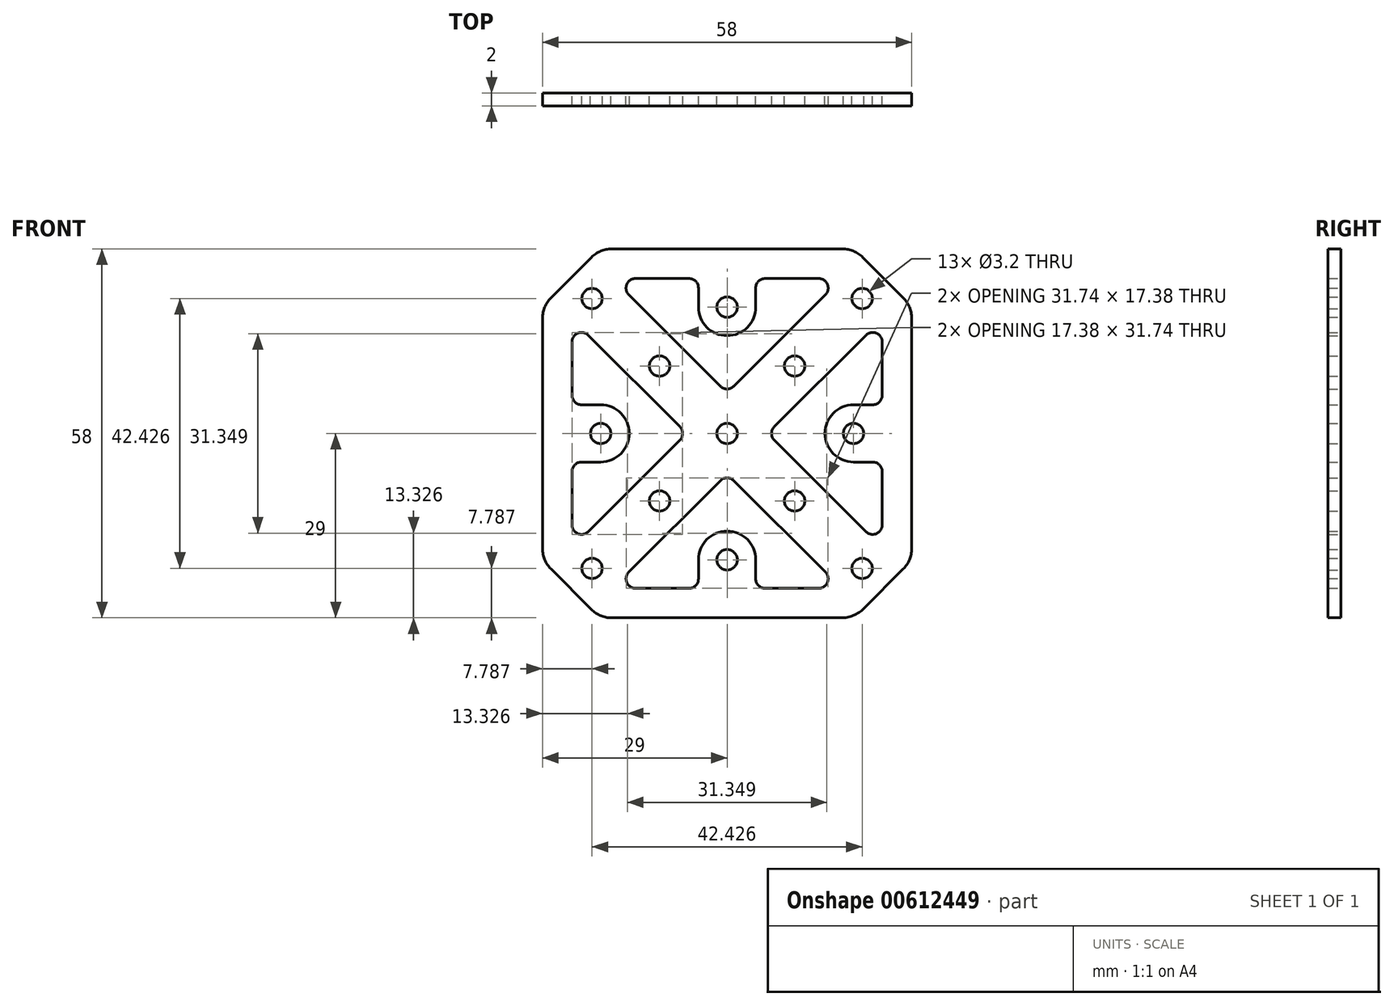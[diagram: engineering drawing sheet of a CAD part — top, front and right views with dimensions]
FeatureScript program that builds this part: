
annotation { "Feature Type Name" : "Feature", "Feature Type Description" : "" }
export const myFeature = defineFeature(function(context is Context, id is Id, definition is map)
    precondition{}
    {
        {
            var Q0;
            Q0=qCreatedBy(makeId("Front.planeOp"),FACE);
            var sketch = newSketch(context, id + "F0", { "sketchPlane" : qUnion([Q0])});
            skLineSegment(sketch, "E0.bottom", {"start": v(0, 0) * mm, "end": v(58, 0) * mm, "construction": true});
            skLineSegment(sketch, "E0.top", {"start": v(0, 58) * mm, "end": v(58, 58) * mm, "construction": true});
            skLineSegment(sketch, "E0.left", {"start": v(0, 0) * mm, "end": v(0, 58) * mm, "construction": true});
            skLineSegment(sketch, "E0.right", {"start": v(58, 0) * mm, "end": v(58, 58) * mm, "construction": true});
            skLineSegment(sketch, "E1", {"start": v(0, 58) * mm, "end": v(58, 0) * mm, "construction": true});
            skCircle(sketch, "E2", {"center": v(29, 29) * mm, "radius": 1.6 * mm});
            skCircle(sketch, "E3", {"center": v(39.6, 18.4) * mm, "radius": 1.6 * mm});
            skCircle(sketch, "E4", {"center": v(50.21, 7.79) * mm, "radius": 1.6 * mm});
            skLineSegment(sketch, "E5", {"start": v(29, 29) * mm, "end": v(29, 0) * mm, "construction": true});
            skLineSegment(sketch, "E6", {"start": v(58, 9) * mm, "end": v(49, 0) * mm, "construction": true});
            skLineSegment(sketch, "E7.MirrorCS", {"start": v(0, 9) * mm, "end": v(9, 0) * mm, "construction": true});
            skLineSegment(sketch, "E8", {"start": v(29, 22.64) * mm, "end": v(47, 4.64) * mm, "construction": true});
            skLineSegment(sketch, "E9", {"start": v(47, 4.64) * mm, "end": v(29, 4.64) * mm, "construction": true});
            skLineSegment(sketch, "E10", {"start": v(29, 4.64) * mm, "end": v(29, 22.64) * mm});
            skLineSegment(sketch, "E11.MirrorCS", {"start": v(11, 4.64) * mm, "end": v(29, 4.64) * mm, "construction": true});
            skLineSegment(sketch, "E12.MirrorCS", {"start": v(29, 22.64) * mm, "end": v(11, 4.64) * mm, "construction": true});
            skLineSegment(sketch, "E13", {"start": v(29, 29) * mm, "end": v(0, 29) * mm, "construction": true});
            skLineSegment(sketch, "E14.MirrorCS", {"start": v(0, 49) * mm, "end": v(9, 58) * mm, "construction": true});
            skLineSegment(sketch, "E15.MirrorCS", {"start": v(58, 49) * mm, "end": v(49, 58) * mm, "construction": true});
            skLineSegment(sketch, "E16", {"start": v(24.5, 9.14) * mm, "end": v(24.5, 4.64) * mm, "construction": true});
            skLineSegment(sketch, "E17", {"start": v(33.5, 9.14) * mm, "end": v(33.5, 4.64) * mm, "construction": true});
            skArc(sketch, "E18", {"start": v(24.5, 9.14) * mm, "mid": v(29, 4.64) * mm, "end": v(33.5, 9.14) * mm, "construction": true});
            skArc(sketch, "E19", {"start": v(33.5, 9.14) * mm, "mid": v(29, 13.64) * mm, "end": v(24.5, 9.14) * mm, "construction": true});
            skCircle(sketch, "E20", {"center": v(29, 9.14) * mm, "radius": 1.6 * mm});
            skSolve(sketch);
        }
        {
            var Q0;
            Q0=qCreatedBy(makeId("Front.planeOp"),FACE);
            var sketch = newSketch(context, id + "F1", { "sketchPlane" : qUnion([Q0])});
            skLineSegment(sketch, "E21.0", {"start": v(10.86, 58) * mm, "end": v(47.14, 58) * mm});
            skLineSegment(sketch, "E21.1", {"start": v(1.32, 50.32) * mm, "end": v(7.68, 56.68) * mm});
            skLineSegment(sketch, "E21.2", {"start": v(0, 10.86) * mm, "end": v(0, 47.14) * mm});
            skLineSegment(sketch, "E21.3", {"start": v(1.32, 7.68) * mm, "end": v(7.68, 1.32) * mm});
            skLineSegment(sketch, "E21.4", {"start": v(10.86, 0) * mm, "end": v(46.93, 0) * mm});
            skLineSegment(sketch, "E21.5", {"start": v(56.68, 7.68) * mm, "end": v(50.46, 1.46) * mm});
            skLineSegment(sketch, "E21.6", {"start": v(58, 10.86) * mm, "end": v(58, 47.14) * mm});
            skCircle(sketch, "E21.7", {"center": v(50.21, 7.79) * mm, "radius": 1.6 * mm});
            skCircle(sketch, "E21.8", {"center": v(39.6, 18.4) * mm, "radius": 1.6 * mm});
            skCircle(sketch, "E21.9", {"center": v(29, 29) * mm, "radius": 1.6 * mm});
            skArc(sketch, "E21.10", {"start": v(33.5, 9.14) * mm, "mid": v(29, 13.64) * mm, "end": v(24.5, 9.14) * mm});
            skLineSegment(sketch, "E21.11", {"start": v(24.5, 9.14) * mm, "end": v(24.5, 6.14) * mm});
            skLineSegment(sketch, "E21.12", {"start": v(33.5, 9.14) * mm, "end": v(33.5, 6.14) * mm});
            skLineSegment(sketch, "E21.13", {"start": v(43.38, 4.64) * mm, "end": v(35, 4.64) * mm});
            skLineSegment(sketch, "E21.14", {"start": v(30.06, 21.58) * mm, "end": v(44.44, 7.2) * mm});
            skLineSegment(sketch, "E21.15", {"start": v(27.94, 21.58) * mm, "end": v(13.56, 7.2) * mm});
            skLineSegment(sketch, "E21.16", {"start": v(14.62, 4.64) * mm, "end": v(23, 4.64) * mm});
            skPoint(sketch, "E22.orphan", {"position": v(0, 58) * mm});
            skLineSegment(sketch, "E23.0", {"start": v(56.68, 50.32) * mm, "end": v(50.32, 56.68) * mm});
            skPoint(sketch, "E24.orphan", {"position": v(58, 58) * mm});
            skPoint(sketch, "E25.orphan", {"position": v(58, 0) * mm});
            skPoint(sketch, "E26.orphan", {"position": v(0, 0) * mm});
            skPoint(sketch, "E27.visualSharp", {"position": v(47, 4.64) * mm});
            skArc(sketch, "E27.filletArc", {"start": v(43.38, 4.64) * mm, "mid": v(44.76, 5.56) * mm, "end": v(44.44, 7.2) * mm});
            skPoint(sketch, "E28.visualSharp", {"position": v(29, 22.64) * mm});
            skArc(sketch, "E28.filletArc", {"start": v(30.06, 21.58) * mm, "mid": v(29, 22.02) * mm, "end": v(27.94, 21.58) * mm});
            skPoint(sketch, "E29.visualSharp", {"position": v(11, 4.64) * mm});
            skArc(sketch, "E29.filletArc", {"start": v(13.56, 7.2) * mm, "mid": v(13.24, 5.56) * mm, "end": v(14.62, 4.64) * mm});
            skPoint(sketch, "E30.newPointA", {"position": v(24.5, 4.64) * mm});
            skPoint(sketch, "E30.newPointB", {"position": v(29, 4.64) * mm});
            skArc(sketch, "E30.filletArc", {"start": v(23, 4.64) * mm, "mid": v(24.06, 5.08) * mm, "end": v(24.5, 6.14) * mm});
            skPoint(sketch, "E31.newPointA", {"position": v(33.5, 4.64) * mm});
            skArc(sketch, "E31.filletArc", {"start": v(33.5, 6.14) * mm, "mid": v(33.94, 5.08) * mm, "end": v(35, 4.64) * mm});
            skPoint(sketch, "E32.visualSharp", {"position": v(49, 0) * mm});
            skArc(sketch, "E32.filletArc", {"start": v(46.93, 0) * mm, "mid": v(48.84, 0.38) * mm, "end": v(50.46, 1.46) * mm});
            skPoint(sketch, "E33.visualSharp", {"position": v(58, 9) * mm});
            skArc(sketch, "E33.filletArc", {"start": v(56.68, 7.68) * mm, "mid": v(57.66, 9.14) * mm, "end": v(58, 10.86) * mm});
            skPoint(sketch, "E34.visualSharp", {"position": v(58, 49) * mm});
            skArc(sketch, "E34.filletArc", {"start": v(58, 47.14) * mm, "mid": v(57.66, 48.86) * mm, "end": v(56.68, 50.32) * mm});
            skPoint(sketch, "E35.visualSharp", {"position": v(49, 58) * mm});
            skArc(sketch, "E35.filletArc", {"start": v(50.32, 56.68) * mm, "mid": v(48.86, 57.66) * mm, "end": v(47.14, 58) * mm});
            skPoint(sketch, "E36.visualSharp", {"position": v(9, 58) * mm});
            skArc(sketch, "E36.filletArc", {"start": v(10.86, 58) * mm, "mid": v(9.14, 57.66) * mm, "end": v(7.68, 56.68) * mm});
            skPoint(sketch, "E37.visualSharp", {"position": v(0, 49) * mm});
            skArc(sketch, "E37.filletArc", {"start": v(1.32, 50.32) * mm, "mid": v(0.34, 48.86) * mm, "end": v(0, 47.14) * mm});
            skPoint(sketch, "E38.visualSharp", {"position": v(0, 9) * mm});
            skArc(sketch, "E38.filletArc", {"start": v(0, 10.86) * mm, "mid": v(0.34, 9.14) * mm, "end": v(1.32, 7.68) * mm});
            skPoint(sketch, "E39.visualSharp", {"position": v(9, 0) * mm});
            skArc(sketch, "E39.filletArc", {"start": v(7.68, 1.32) * mm, "mid": v(9.14, 0.34) * mm, "end": v(10.86, 0) * mm});
            skCircle(sketch, "E40.0", {"center": v(29, 9.14) * mm, "radius": 1.6 * mm});
            skCircle(sketch, "E41.1.0", {"center": v(39.6, 39.6) * mm, "radius": 1.6 * mm});
            skCircle(sketch, "E41.1.1", {"center": v(50.21, 50.21) * mm, "radius": 1.6 * mm});
            skArc(sketch, "E41.1.2", {"start": v(53.36, 43.38) * mm, "mid": v(52.44, 44.76) * mm, "end": v(50.8, 44.44) * mm});
            skLineSegment(sketch, "E41.1.3", {"start": v(36.42, 30.06) * mm, "end": v(50.8, 44.44) * mm});
            skLineSegment(sketch, "E41.1.4", {"start": v(53.36, 43.38) * mm, "end": v(53.36, 35) * mm});
            skArc(sketch, "E41.1.5", {"start": v(51.86, 33.5) * mm, "mid": v(52.92, 33.94) * mm, "end": v(53.36, 35) * mm});
            skLineSegment(sketch, "E41.1.6", {"start": v(48.86, 33.5) * mm, "end": v(51.86, 33.5) * mm});
            skArc(sketch, "E41.1.7", {"start": v(48.86, 33.5) * mm, "mid": v(44.36, 29) * mm, "end": v(48.86, 24.5) * mm});
            skCircle(sketch, "E41.1.8", {"center": v(48.86, 29) * mm, "radius": 1.6 * mm});
            skLineSegment(sketch, "E41.1.9", {"start": v(48.86, 24.5) * mm, "end": v(51.86, 24.5) * mm});
            skArc(sketch, "E41.1.10", {"start": v(53.36, 23) * mm, "mid": v(52.92, 24.06) * mm, "end": v(51.86, 24.5) * mm});
            skLineSegment(sketch, "E41.1.11", {"start": v(53.36, 14.62) * mm, "end": v(53.36, 23) * mm});
            skArc(sketch, "E41.1.12", {"start": v(50.8, 13.56) * mm, "mid": v(52.44, 13.24) * mm, "end": v(53.36, 14.62) * mm});
            skLineSegment(sketch, "E41.1.13", {"start": v(36.42, 27.94) * mm, "end": v(50.8, 13.56) * mm});
            skArc(sketch, "E41.1.14", {"start": v(36.42, 30.06) * mm, "mid": v(35.98, 29) * mm, "end": v(36.42, 27.94) * mm});
            skCircle(sketch, "E41.2.0", {"center": v(18.4, 39.6) * mm, "radius": 1.6 * mm});
            skCircle(sketch, "E41.2.1", {"center": v(7.79, 50.21) * mm, "radius": 1.6 * mm});
            skArc(sketch, "E41.2.2", {"start": v(14.62, 53.36) * mm, "mid": v(13.24, 52.44) * mm, "end": v(13.56, 50.8) * mm});
            skLineSegment(sketch, "E41.2.3", {"start": v(27.94, 36.42) * mm, "end": v(13.56, 50.8) * mm});
            skLineSegment(sketch, "E41.2.4", {"start": v(14.62, 53.36) * mm, "end": v(23, 53.36) * mm});
            skArc(sketch, "E41.2.5", {"start": v(24.5, 51.86) * mm, "mid": v(24.06, 52.92) * mm, "end": v(23, 53.36) * mm});
            skLineSegment(sketch, "E41.2.6", {"start": v(24.5, 48.86) * mm, "end": v(24.5, 51.86) * mm});
            skArc(sketch, "E41.2.7", {"start": v(24.5, 48.86) * mm, "mid": v(29, 44.36) * mm, "end": v(33.5, 48.86) * mm});
            skCircle(sketch, "E41.2.8", {"center": v(29, 48.86) * mm, "radius": 1.6 * mm});
            skLineSegment(sketch, "E41.2.9", {"start": v(33.5, 48.86) * mm, "end": v(33.5, 51.86) * mm});
            skArc(sketch, "E41.2.10", {"start": v(35, 53.36) * mm, "mid": v(33.94, 52.92) * mm, "end": v(33.5, 51.86) * mm});
            skLineSegment(sketch, "E41.2.11", {"start": v(43.38, 53.36) * mm, "end": v(35, 53.36) * mm});
            skArc(sketch, "E41.2.12", {"start": v(44.44, 50.8) * mm, "mid": v(44.76, 52.44) * mm, "end": v(43.38, 53.36) * mm});
            skLineSegment(sketch, "E41.2.13", {"start": v(30.06, 36.42) * mm, "end": v(44.44, 50.8) * mm});
            skArc(sketch, "E41.2.14", {"start": v(27.94, 36.42) * mm, "mid": v(29, 35.98) * mm, "end": v(30.06, 36.42) * mm});
            skCircle(sketch, "E41.3.0", {"center": v(18.4, 18.4) * mm, "radius": 1.6 * mm});
            skCircle(sketch, "E41.3.1", {"center": v(7.79, 7.79) * mm, "radius": 1.6 * mm});
            skArc(sketch, "E41.3.2", {"start": v(4.64, 14.62) * mm, "mid": v(5.56, 13.24) * mm, "end": v(7.2, 13.56) * mm});
            skLineSegment(sketch, "E41.3.3", {"start": v(21.58, 27.94) * mm, "end": v(7.2, 13.56) * mm});
            skLineSegment(sketch, "E41.3.4", {"start": v(4.64, 14.62) * mm, "end": v(4.64, 23) * mm});
            skArc(sketch, "E41.3.5", {"start": v(6.14, 24.5) * mm, "mid": v(5.08, 24.06) * mm, "end": v(4.64, 23) * mm});
            skLineSegment(sketch, "E41.3.6", {"start": v(9.14, 24.5) * mm, "end": v(6.14, 24.5) * mm});
            skArc(sketch, "E41.3.7", {"start": v(9.14, 24.5) * mm, "mid": v(13.64, 29) * mm, "end": v(9.14, 33.5) * mm});
            skCircle(sketch, "E41.3.8", {"center": v(9.14, 29) * mm, "radius": 1.6 * mm});
            skLineSegment(sketch, "E41.3.9", {"start": v(9.14, 33.5) * mm, "end": v(6.14, 33.5) * mm});
            skArc(sketch, "E41.3.10", {"start": v(4.64, 35) * mm, "mid": v(5.08, 33.94) * mm, "end": v(6.14, 33.5) * mm});
            skLineSegment(sketch, "E41.3.11", {"start": v(4.64, 43.38) * mm, "end": v(4.64, 35) * mm});
            skArc(sketch, "E41.3.12", {"start": v(7.2, 44.44) * mm, "mid": v(5.56, 44.76) * mm, "end": v(4.64, 43.38) * mm});
            skLineSegment(sketch, "E41.3.13", {"start": v(21.58, 30.06) * mm, "end": v(7.2, 44.44) * mm});
            skArc(sketch, "E41.3.14", {"start": v(21.58, 27.94) * mm, "mid": v(22.02, 29) * mm, "end": v(21.58, 30.06) * mm});
            skSolve(sketch);
        }
        {
            var Q0;
            Q0=makeQuery(id+"F1.imprint","IMPRINT",FACE,{"disambiguationData":[TD([[makeQuery(id+"F1.imprint","IMPRINT",EDGE,{"derivedFrom":sQuery(id+"F1.wireOp",EDGE,"E21.0")}),-1.0]])]});
            extrude(context, id + "F2", {"entities" : qUnion([Q0]), "depth" : 2 * mm, "offsetDistance" : 25 * mm});
        }
    });
